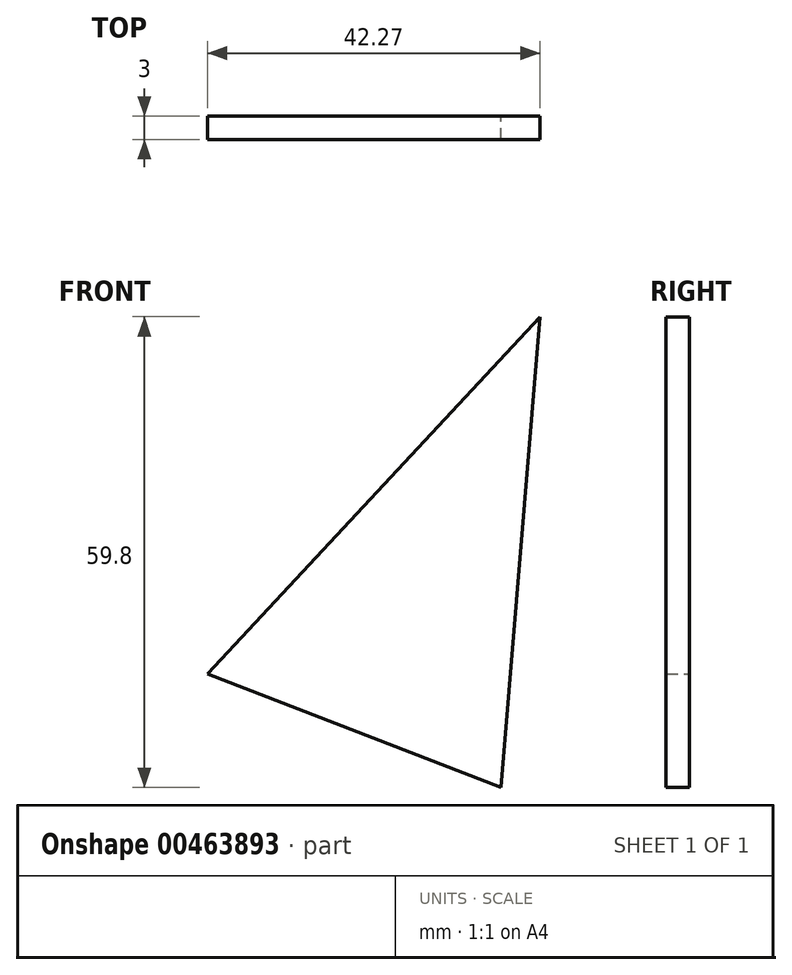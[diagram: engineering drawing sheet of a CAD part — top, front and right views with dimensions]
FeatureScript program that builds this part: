
annotation { "Feature Type Name" : "Feature", "Feature Type Description" : "" }
export const myFeature = defineFeature(function(context is Context, id is Id, definition is map)
    precondition{}
    {
        {
            var Q0;
            Q0=qCreatedBy(makeId("Front.planeOp"),FACE);
            var sketch = newSketch(context, id + "F0", { "sketchPlane" : qUnion([Q0])});
            skLineSegment(sketch, "E0", {"start": v(0, 0) * mm, "end": v(42.27, 45.36) * mm});
            skLineSegment(sketch, "E1", {"start": v(42.27, 45.36) * mm, "end": v(37.3, -14.44) * mm});
            skLineSegment(sketch, "E2", {"start": v(37.3, -14.44) * mm, "end": v(0, 0) * mm});
            skSolve(sketch);
        }
        {
            var Q0;
            Q0=makeQuery(id+"F0.imprint","IMPRINT",FACE,{"disambiguationData":[TD([[makeQuery(id+"F0.imprint","IMPRINT",EDGE,{"derivedFrom":sQuery(id+"F0.wireOp",EDGE,"E0")}),-1.0]])]});
            extrude(context, id + "F1", {"entities" : qUnion([Q0]), "depth" : 3 * mm});
        }
    });
